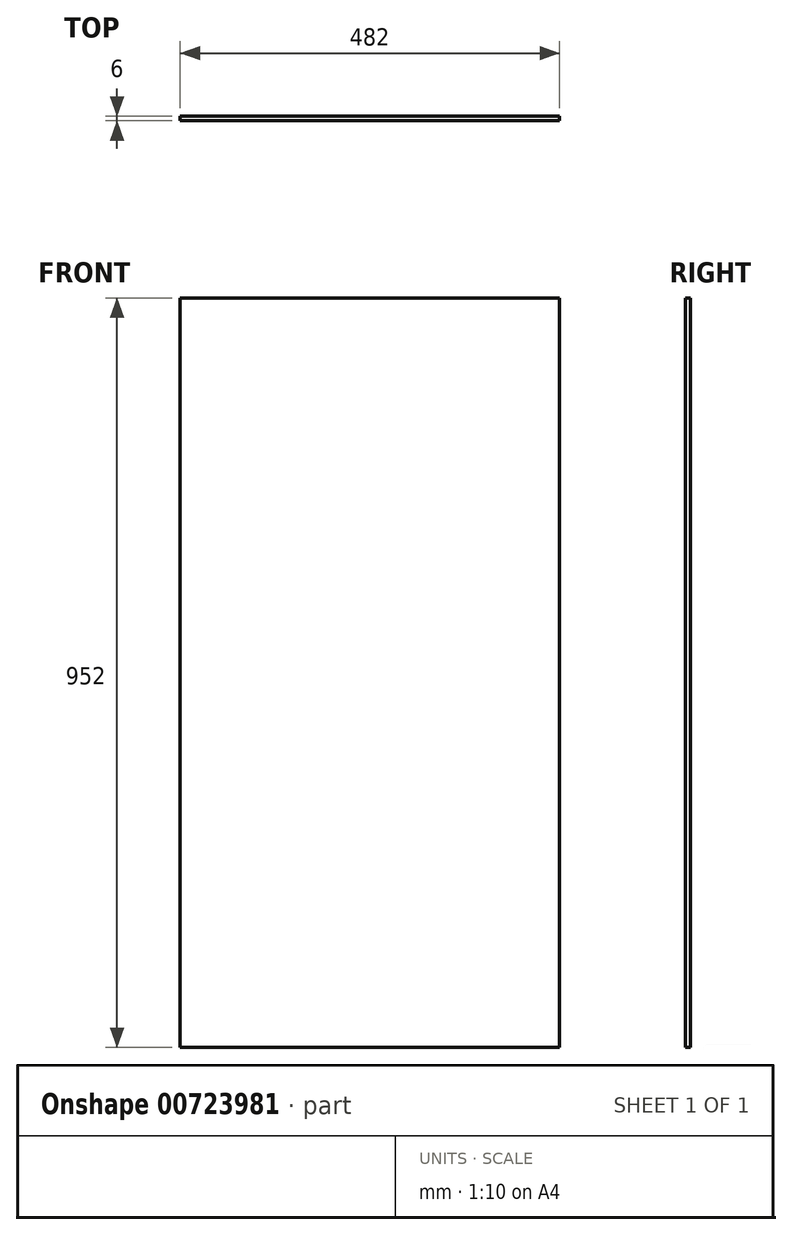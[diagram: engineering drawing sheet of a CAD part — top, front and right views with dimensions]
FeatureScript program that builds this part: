
annotation { "Feature Type Name" : "Feature", "Feature Type Description" : "" }
export const myFeature = defineFeature(function(context is Context, id is Id, definition is map)
    precondition{}
    {
        {
            var Q0;
            Q0=qCreatedBy(makeId("Front.planeOp"),FACE);
            var sketch = newSketch(context, id + "F0", { "sketchPlane" : qUnion([Q0])});
            skLineSegment(sketch, "E0.bottom", {"start": v(-350.74, 451.04) * mm, "end": v(131.26, 451.04) * mm});
            skLineSegment(sketch, "E0.top", {"start": v(-350.74, -500.96) * mm, "end": v(131.26, -500.96) * mm});
            skLineSegment(sketch, "E0.left", {"start": v(-350.74, 451.04) * mm, "end": v(-350.74, -500.96) * mm});
            skLineSegment(sketch, "E0.right", {"start": v(131.26, 451.04) * mm, "end": v(131.26, -500.96) * mm});
            skSolve(sketch);
        }
        {
            var Q0;
            Q0=qSketchRegion(id+"F0",true);
            extrude(context, id + "F1", {"entities" : qUnion([Q0]), "depth" : 6 * mm, "offsetDistance" : 25 * mm});
        }
    });
